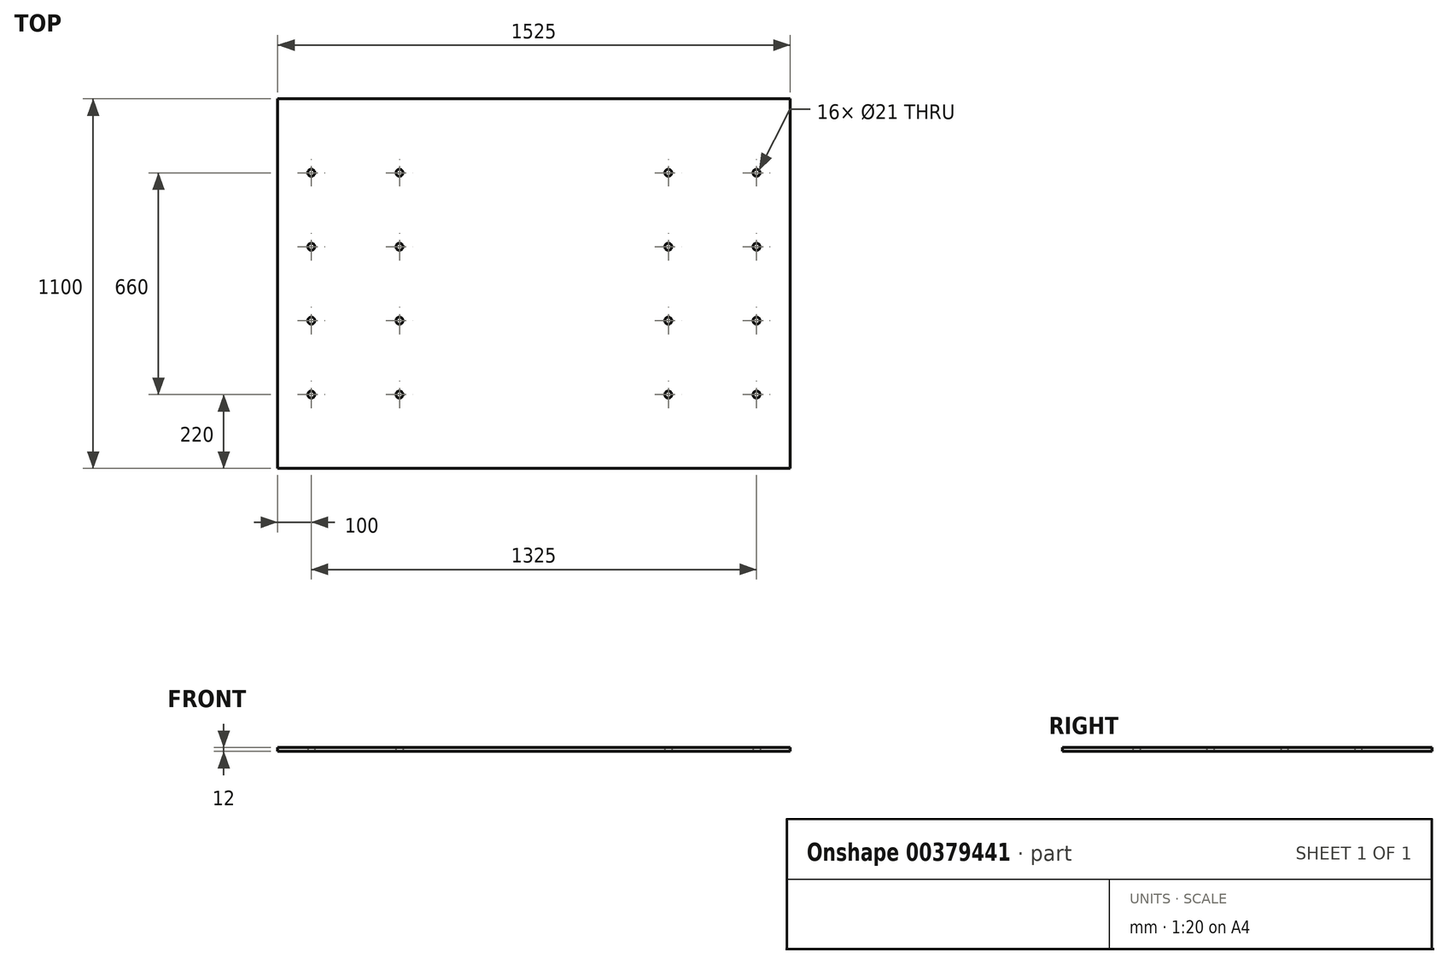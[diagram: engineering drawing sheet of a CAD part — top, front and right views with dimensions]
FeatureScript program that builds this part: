
annotation { "Feature Type Name" : "Feature", "Feature Type Description" : "" }
export const myFeature = defineFeature(function(context is Context, id is Id, definition is map)
    precondition{}
    {
        {
            var Q0;
            Q0=qCreatedBy(makeId("Top.planeOp"),FACE);
            var sketch = newSketch(context, id + "F0", { "sketchPlane" : qUnion([Q0])});
            skLineSegment(sketch, "E0.bottom", {"start": v(762.5, -550) * mm, "end": v(-762.5, -550) * mm});
            skLineSegment(sketch, "E0.top", {"start": v(762.5, 550) * mm, "end": v(-762.5, 550) * mm});
            skLineSegment(sketch, "E0.left", {"start": v(762.5, -550) * mm, "end": v(762.5, 550) * mm});
            skLineSegment(sketch, "E0.right", {"start": v(-762.5, -550) * mm, "end": v(-762.5, 550) * mm});
            skPoint(sketch, "E0.middle", {"position": v(0, 0) * mm});
            skCircle(sketch, "E1", {"center": v(662.5, 330) * mm, "radius": 10.5 * mm});
            skCircle(sketch, "E2", {"center": v(662.5, 110) * mm, "radius": 10.5 * mm});
            skCircle(sketch, "E3", {"center": v(662.5, -110) * mm, "radius": 10.5 * mm});
            skCircle(sketch, "E4", {"center": v(662.5, -330) * mm, "radius": 10.5 * mm});
            skLineSegment(sketch, "E5", {"start": v(662.5, 330) * mm, "end": v(662.5, -422.18) * mm, "construction": true});
            skLineSegment(sketch, "E6", {"start": v(0, 550) * mm, "end": v(0, -550) * mm, "construction": true});
            skLineSegment(sketch, "E7.0", {"start": v(-400, 550) * mm, "end": v(-400, -550) * mm, "construction": true});
            skLineSegment(sketch, "E8.0", {"start": v(400, 550) * mm, "end": v(400, -550) * mm, "construction": true});
            skCircle(sketch, "E9", {"center": v(400, 330) * mm, "radius": 10.5 * mm});
            skCircle(sketch, "E10", {"center": v(400, 110) * mm, "radius": 10.5 * mm});
            skCircle(sketch, "E11", {"center": v(400, -110) * mm, "radius": 10.5 * mm});
            skCircle(sketch, "E12", {"center": v(400, -330) * mm, "radius": 10.5 * mm});
            skCircle(sketch, "E13.MirrorC", {"center": v(-400, 330) * mm, "radius": 10.5 * mm});
            skCircle(sketch, "E14.MirrorC", {"center": v(-662.5, 330) * mm, "radius": 10.5 * mm});
            skCircle(sketch, "E15.MirrorC", {"center": v(-400, 110) * mm, "radius": 10.5 * mm});
            skCircle(sketch, "E16.MirrorC", {"center": v(-662.5, 110) * mm, "radius": 10.5 * mm});
            skCircle(sketch, "E17.MirrorC", {"center": v(-400, -110) * mm, "radius": 10.5 * mm});
            skCircle(sketch, "E18.MirrorC", {"center": v(-662.5, -110) * mm, "radius": 10.5 * mm});
            skCircle(sketch, "E19.MirrorC", {"center": v(-400, -330) * mm, "radius": 10.5 * mm});
            skCircle(sketch, "E20.MirrorC", {"center": v(-662.5, -330) * mm, "radius": 10.5 * mm});
            skSolve(sketch);
        }
        {
            var Q0;
            Q0=makeQuery(id+"F0.imprint","IMPRINT",FACE,{"disambiguationData":[TD([[makeQuery(id+"F0.imprint","IMPRINT",EDGE,{"derivedFrom":sQuery(id+"F0.wireOp",EDGE,"E0.bottom")}),-1.0]])]});
            extrude(context, id + "F1", {"entities" : qUnion([Q0]), "depth" : 12 * mm});
        }
    });
